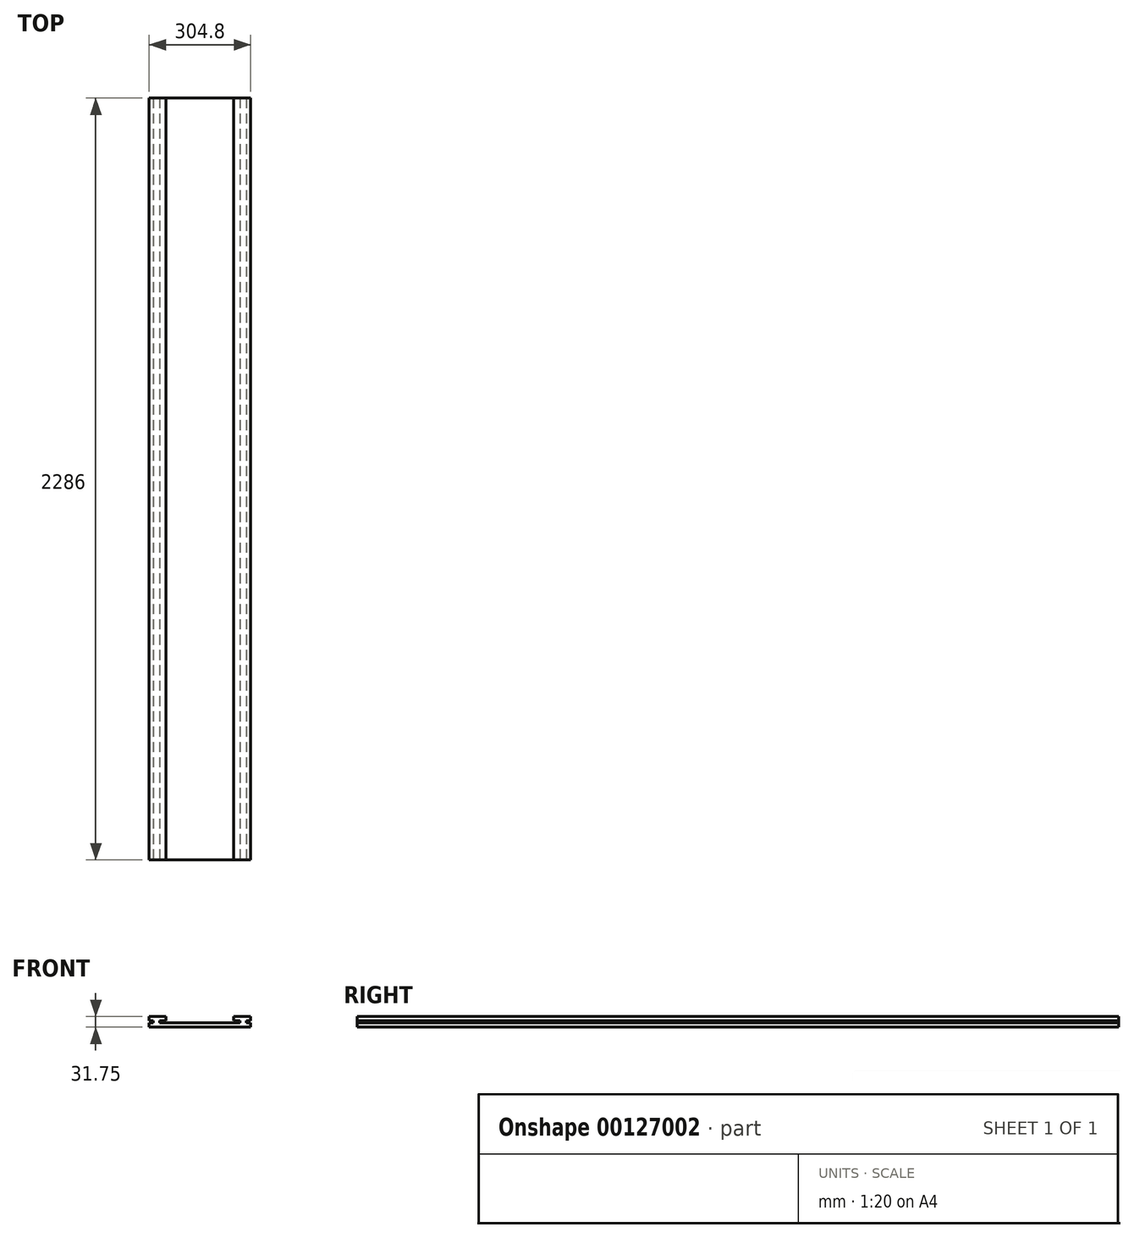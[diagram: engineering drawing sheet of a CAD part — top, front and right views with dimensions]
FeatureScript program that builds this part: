
annotation { "Feature Type Name" : "Feature", "Feature Type Description" : "" }
export const myFeature = defineFeature(function(context is Context, id is Id, definition is map)
    precondition{}
    {
        {
            var Q0;
            Q0=qCreatedBy(makeId("Front.planeOp"),FACE);
            var sketch = newSketch(context, id + "F0", { "sketchPlane" : qUnion([Q0])});
            skLineSegment(sketch, "E0", {"start": v(-35.06, -12.7) * mm, "end": v(269.74, -12.7) * mm});
            skLineSegment(sketch, "E1", {"start": v(-35.06, -12.7) * mm, "end": v(-35.06, 0) * mm});
            skLineSegment(sketch, "E2", {"start": v(269.74, -12.7) * mm, "end": v(269.74, 0) * mm});
            skLineSegment(sketch, "E3", {"start": v(-35.06, 19.05) * mm, "end": v(15.74, 19.05) * mm});
            skLineSegment(sketch, "E4", {"start": v(269.74, 19.05) * mm, "end": v(218.94, 19.05) * mm});
            skLineSegment(sketch, "E5", {"start": v(15.74, 19.05) * mm, "end": v(15.74, 6.35) * mm});
            skLineSegment(sketch, "E6", {"start": v(218.94, 19.05) * mm, "end": v(218.94, 6.35) * mm});
            skLineSegment(sketch, "E7", {"start": v(15.74, 6.35) * mm, "end": v(-3.31, 6.35) * mm});
            skLineSegment(sketch, "E8", {"start": v(218.94, 6.35) * mm, "end": v(237.99, 6.35) * mm});
            skLineSegment(sketch, "E9", {"start": v(-3.31, 6.35) * mm, "end": v(-3.31, 0) * mm});
            skLineSegment(sketch, "E10", {"start": v(237.99, 6.35) * mm, "end": v(237.99, 0) * mm});
            skLineSegment(sketch, "E11", {"start": v(-3.31, 0) * mm, "end": v(237.99, 0) * mm});
            skLineSegment(sketch, "E12", {"start": v(-35.06, 0) * mm, "end": v(-22.36, 0) * mm});
            skLineSegment(sketch, "E13", {"start": v(-22.36, 0) * mm, "end": v(-22.36, 6.35) * mm});
            skLineSegment(sketch, "E14", {"start": v(-22.36, 6.35) * mm, "end": v(-35.06, 6.35) * mm});
            skLineSegment(sketch, "E15.trimOffspring", {"start": v(-35.06, 6.35) * mm, "end": v(-35.06, 19.05) * mm});
            skLineSegment(sketch, "E16", {"start": v(269.74, 0) * mm, "end": v(257.04, 0) * mm});
            skLineSegment(sketch, "E17", {"start": v(257.04, 0) * mm, "end": v(257.04, 6.35) * mm});
            skLineSegment(sketch, "E18", {"start": v(257.04, 6.35) * mm, "end": v(269.74, 6.35) * mm});
            skLineSegment(sketch, "E19.trimOffspring", {"start": v(269.74, 6.35) * mm, "end": v(269.74, 19.05) * mm});
            skSolve(sketch);
        }
        {
            var Q0;
            Q0 = qSketchRegion(id + "F0", true);
            extrude(context, id + "F1", {"entities" : qUnion([Q0]), "oppositeDirection" : true, "depth" : 2286 * mm});
        }
    });
